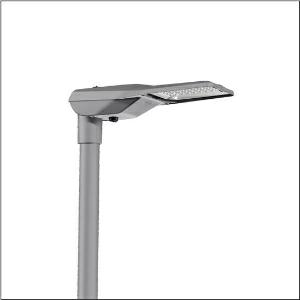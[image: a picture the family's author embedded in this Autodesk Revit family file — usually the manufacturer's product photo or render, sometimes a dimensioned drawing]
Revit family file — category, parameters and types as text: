
# Revit family: streetlight_sl_21_iq_mini___st1_0ab_5xe2m31y08gb_c9fc
name_source: partatom
category: Lighting Fixtures
units: mm (PartAtom-declared; Revit-internal decimal feet)

## family parameters
Cut with Voids When Loaded = No
Host = Face
Light Source = No
Part Type = Normal
Room Calculation Point = No
Round Connector Dimension = Use Diameter
Shared = No

## types (1)
- --- (1 x LED, 5270 lm, 39.8 W, 3000K)
    Apparent Load = 40 VA
    CIE Flux Codes = 38 73 97 100 100
    Color Rendering = 70
    Color Temperature = 3000K
    Default Elevation = 1800 mm
    Description = Streetlight SL 21 iQ mini, mast luminaire, primary light control with lens, of PMMA, primary optical cover: cover, of toughened safety glass, transparent, light distribution: ST1.0aB, light emission: direct distribution, primary light characteristic: asymmetric, installation type: post-top, side-entry, LED, High Power LED, rated luminous flux: 5.270lm, luminous efficacy: 132lm/W, light colour: 730, colour temperature: 3000K, control: presetting dimming logarithmic, Street-Remote, Auto-Match, Temp-Guard, Lumen-Switch, Night-Set, Smart-Wire, Light-Fading, Desk-Remote (wireless, voltage-free reading and setting of iQ features in the workshop via application-optimized NFC function/RFID function), optimised constant luminous flux control (CLO 2.0), mains connection: 220..240V, AC, 50/60Hz, start of lifetime: 40W, end of service life: 41W, reduction: 18W, luminaire housing, of diecast aluminium, powder-coated, Siteco® metallic grey (DB 702S), corrosivity category C5 mid according to DIN EN ISO 12944, please order mast flange separately, inclination adjustable: 0°, 5°, 10°, 15°, sealing non-destructively replaceable, multi-level sealing system, length: 628mm, width: 235mm, height: 110mm, mast flange for spigot size: 42mm (side-entry): 5XC10008XM4, 60/48mm (side-entry/post-top): 5XC10108XM2, 76/60mm (side-entry/post-top): 5XC10108XM1, Smart Interface below and above, protection rating (complete): IP66, insulation class (complete): insulation class II (safety insulation), certification: CE, ENEC, ENEC+, VDE, impact resistance: IK09, permissible operating ambient temperature for outdoor applications: -40..+50°C, standard-compliant lighting for roads and squares, packaging unit: 1 piece

Light Distribution: ST1.0aB
    Height = 110 mm
    Lamp = 1 x LED
    Lamp Light Flux = 5270 lm
    Lamp Power = 39.8 W
    Lamp count = 1
    Length = 625 mm
    Luminous efficacy = 132 lm/W
    Manufacturer = Siteco
    ModVariant = No
    Model = 5XE2M31Y08GB
    Number of Poles = 1
    OnlyDefault = Yes
    Power Factor = 1
    Product Name = Streetlight SL 21 iQ mini | ST1.0aB
    Product group = mast luminaire | pylon top
    ProductGroupID = 6100
    Protection Class = Protection class II
    Protection Degree = IP 66
    RLX_Detail_Level = 1
    RLX_Emergency_Light_Flux = 0 lm
    RLX_Emergency_Type = 0
    RLX_Emergency_Type_DB = No
    RlxData = <blob elided: 92717 chars, md5=f5fbc56b>
    Socket = socket
    Standby Power = 0 W
    System Light Flux = 5270 lm
    System Power = 40 W
    Type Comments = factory setting: luminous flux: 100 % | dim-lin: 254 | 800 mA
    Type Image = l_1003514.jpg
    URL = http://relux.com
    VarID = @adj_042521
    Voltage = 0 V
    Weight = 0.00 kg
    Width = 234 mm

## geometry (parser evidence)
native form markers: Blend x4, Sweep x10
no freeform markers — native parametric forms only
